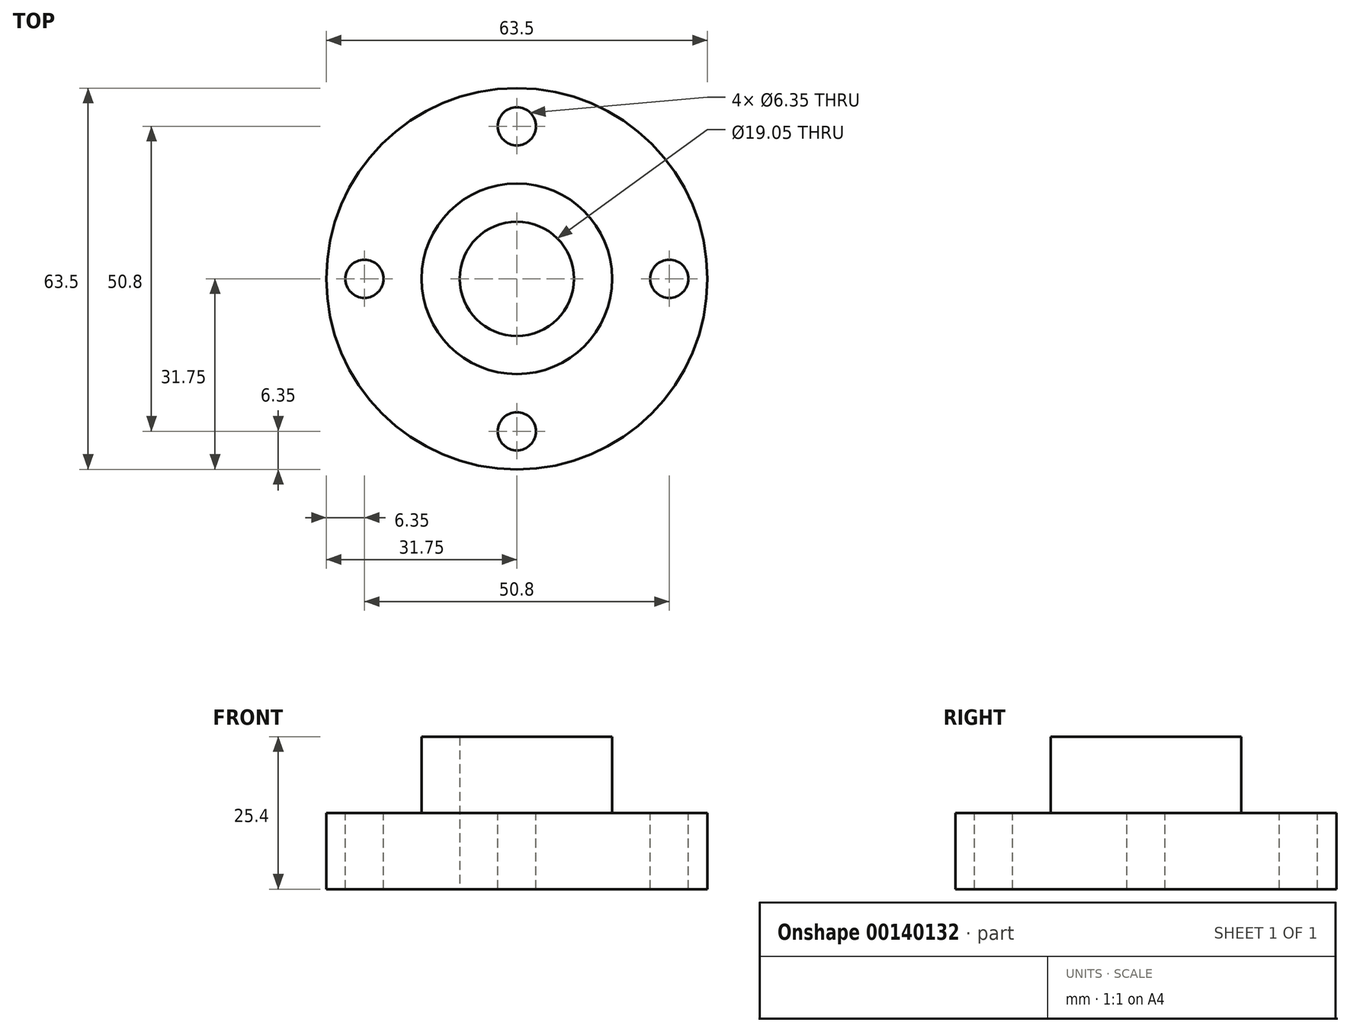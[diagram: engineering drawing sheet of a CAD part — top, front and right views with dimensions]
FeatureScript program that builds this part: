
annotation { "Feature Type Name" : "Feature", "Feature Type Description" : "" }
export const myFeature = defineFeature(function(context is Context, id is Id, definition is map)
    precondition{}
    {
        {
            var Q0;
            Q0=qCreatedBy(makeId("Front.planeOp"),FACE);
            var sketch = newSketch(context, id + "F0", { "sketchPlane" : qUnion([Q0])});
            skLineSegment(sketch, "E0", {"start": v(-9.52, 0) * mm, "end": v(-9.52, 25.4) * mm});
            skLineSegment(sketch, "E1", {"start": v(-9.52, 25.4) * mm, "end": v(-15.88, 25.4) * mm});
            skLineSegment(sketch, "E2", {"start": v(-15.88, 25.4) * mm, "end": v(-15.88, 12.7) * mm});
            skLineSegment(sketch, "E3", {"start": v(-15.88, 12.7) * mm, "end": v(-31.75, 12.7) * mm});
            skLineSegment(sketch, "E4", {"start": v(-31.75, 12.7) * mm, "end": v(-31.75, 0) * mm});
            skLineSegment(sketch, "E5", {"start": v(-31.75, 0) * mm, "end": v(-9.53, 0) * mm});
            skLineSegment(sketch, "E6", {"start": v(0, 0) * mm, "end": v(0, 38.71) * mm, "construction": true});
            skSolve(sketch);
        }
        {
            var Q0;
            Q0 = qSketchRegion(id + "F0", true);
            var Q1;
            Q1=sQuery(id+"F0.wireOp",EDGE,"E6");
            revolve(context, id + "F1", {"entities" : qUnion([Q0]), "axis" : qUnion([Q1]), "revolveType" : RevolveType.FULL});
        }
        {
            var Q0;
            Q0=makeQuery(id+"F1.opRevolve","SWEPT_FACE",FACE,{"disambiguationData":[OSD([sQuery(id+"F0.wireOp",EDGE,"E3")])]});
            var sketch = newSketch(context, id + "F2", { "sketchPlane" : qUnion([Q0])});
            skCircle(sketch, "E7", {"center": v(0, 0) * mm, "radius": 25.4 * mm, "construction": true});
            skPoint(sketch, "E8", {"position": v(0, 25.4) * mm});
            skPoint(sketch, "E9", {"position": v(-25.4, 0) * mm});
            skPoint(sketch, "E10", {"position": v(0, -25.4) * mm});
            skPoint(sketch, "E11", {"position": v(25.4, 0) * mm});
            skSolve(sketch);
        }
        {
            var Q0;
            Q0=sQuery(id+"F2.wireOp",VERTEX,"E8");
            var Q1;
            Q1=sQuery(id+"F2.wireOp",VERTEX,"E9");
            var Q2;
            Q2=sQuery(id+"F2.wireOp",VERTEX,"E10");
            var Q3;
            Q3=sQuery(id+"F2.wireOp",VERTEX,"E11");
            var Q4;
            Q4=makeQuery(id+"F1.opRevolve","SWEPT_BODY",BODY,{"disambiguationData":[OSD([sQuery(id+"F0.wireOp",EDGE,"E0"),sQuery(id+"F0.wireOp",EDGE,"E1"),sQuery(id+"F0.wireOp",EDGE,"E2"),sQuery(id+"F0.wireOp",EDGE,"E3"),sQuery(id+"F0.wireOp",EDGE,"E4"),sQuery(id+"F0.wireOp",EDGE,"E5")])]});
            hole(context, id + "F3", {"style" : HoleStyle.SIMPLE, "endStyle" : HoleEndStyle.THROUGH, "holeDiameter" : 6.35 * mm, "locations" : qUnion([Q0, Q1, Q2, Q3]), "scope" : qUnion([Q4]), "isTappedThrough" : true});
        }
    });
